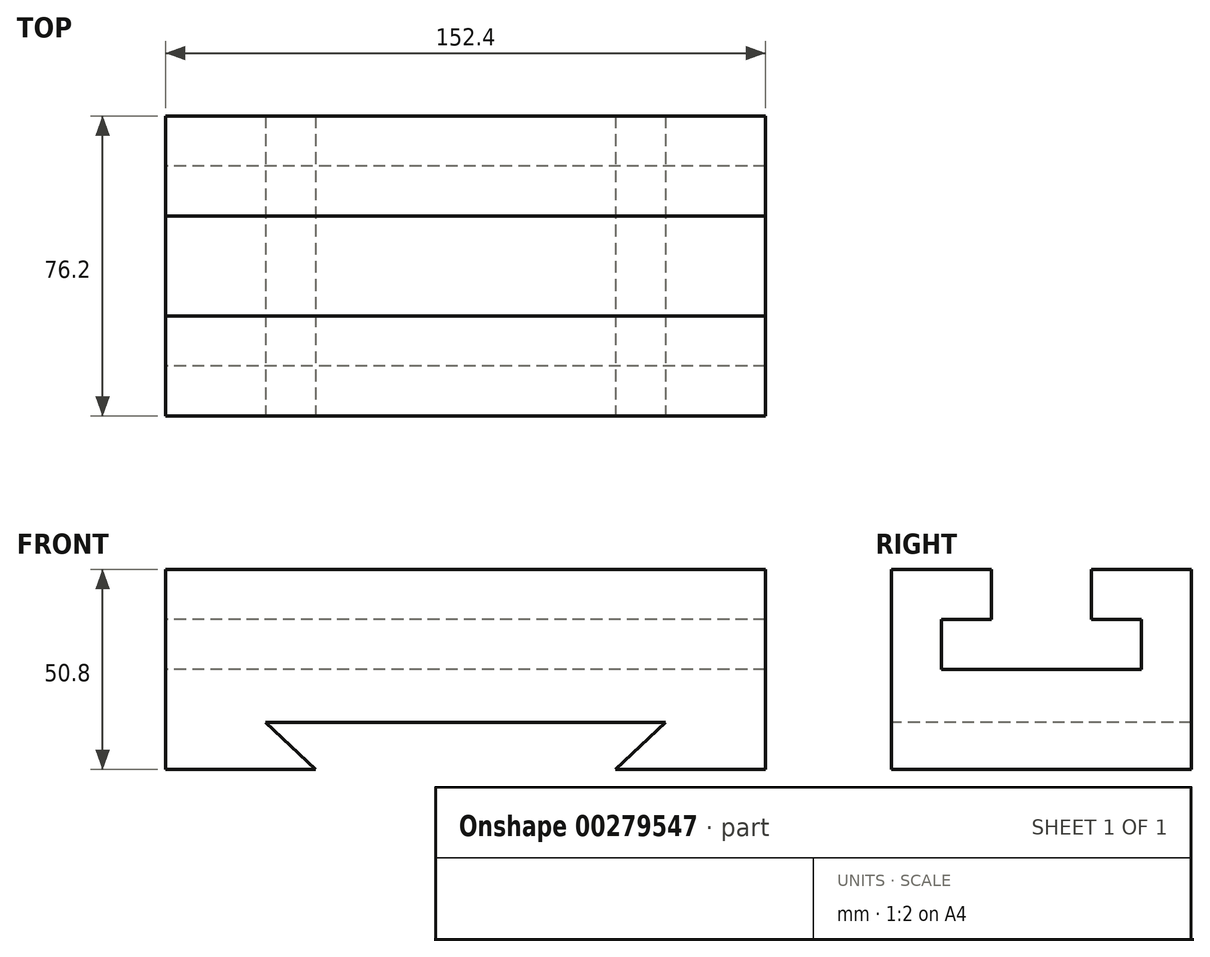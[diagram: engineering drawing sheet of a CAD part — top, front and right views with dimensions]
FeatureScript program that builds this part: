
annotation { "Feature Type Name" : "Feature", "Feature Type Description" : "" }
export const myFeature = defineFeature(function(context is Context, id is Id, definition is map)
    precondition{}
    {
        {
            var Q0;
            Q0=qCreatedBy(makeId("Right.planeOp"),FACE);
            var sketch = newSketch(context, id + "F0", { "sketchPlane" : qUnion([Q0])});
            skLineSegment(sketch, "E0.bottom", {"start": v(-38.1, 25.4) * mm, "end": v(-12.7, 25.4) * mm});
            skLineSegment(sketch, "E0.top", {"start": v(-38.1, -25.4) * mm, "end": v(38.1, -25.4) * mm});
            skLineSegment(sketch, "E0.left", {"start": v(-38.1, 25.4) * mm, "end": v(-38.1, -25.4) * mm});
            skLineSegment(sketch, "E0.right", {"start": v(38.1, 25.4) * mm, "end": v(38.1, -25.4) * mm});
            skPoint(sketch, "E0.middle", {"position": v(0, 0) * mm});
            skPoint(sketch, "E1", {"position": v(0, 25.4) * mm});
            skLineSegment(sketch, "E2", {"start": v(12.7, 25.4) * mm, "end": v(12.7, 12.7) * mm});
            skLineSegment(sketch, "E3", {"start": v(12.7, 12.7) * mm, "end": v(25.4, 12.7) * mm});
            skLineSegment(sketch, "E4", {"start": v(25.4, 12.7) * mm, "end": v(25.4, 0) * mm});
            skLineSegment(sketch, "E5", {"start": v(25.4, 0) * mm, "end": v(-25.4, 0) * mm});
            skLineSegment(sketch, "E6", {"start": v(-25.4, 0) * mm, "end": v(-25.4, 12.7) * mm});
            skLineSegment(sketch, "E7", {"start": v(-25.4, 12.7) * mm, "end": v(-12.7, 12.7) * mm});
            skLineSegment(sketch, "E8", {"start": v(-12.7, 12.7) * mm, "end": v(-12.7, 25.4) * mm});
            skLineSegment(sketch, "E9.trimOffspring", {"start": v(12.7, 25.4) * mm, "end": v(38.1, 25.4) * mm});
            skSolve(sketch);
        }
        {
            var Q0;
            Q0 = qSketchRegion(id + "F0", true);
            extrude(context, id + "F1", {"entities" : qUnion([Q0]), "depth" : 152.4 * mm});
        }
        {
            var Q0;
            Q0=qCreatedBy(makeId("Front.planeOp"),FACE);
            var sketch = newSketch(context, id + "F2", { "sketchPlane" : qUnion([Q0])});
            skPoint(sketch, "E10", {"position": v(76.2, -25.4) * mm});
            skLineSegment(sketch, "E11", {"start": v(38.1, -25.4) * mm, "end": v(114.3, -25.4) * mm});
            skLineSegment(sketch, "E12", {"start": v(93.65, -26.27) * mm, "end": v(93.65, -25.4) * mm});
            skLineSegment(sketch, "E13", {"start": v(38.1, -25.4) * mm, "end": v(25.4, -13.42) * mm});
            skLineSegment(sketch, "E14", {"start": v(25.4, -13.42) * mm, "end": v(127, -13.42) * mm});
            skLineSegment(sketch, "E15", {"start": v(127, -13.42) * mm, "end": v(114.3, -25.4) * mm});
            skPoint(sketch, "E16.orphan", {"position": v(93.65, -13.42) * mm});
            skSolve(sketch);
        }
        {
            var Q0;
            Q0 = qSketchRegion(id + "F2", true);
            extrude(context, id + "F3", {"entities" : qUnion([Q0]), "operationType" : NewBodyOperationType.REMOVE, "oppositeDirection" : true, "depth" : 76.2 * mm});
        }
        {
            var Q0;
            Q0=makeQuery(id+"F3.boolean.opBoolean","COPY",FACE,{"derivedFrom":makeQuery(id+"F3.opExtrude","CAP_FACE",FACE,{"disambiguationData":[OSD([sQuery(id+"F2.wireOp",EDGE,"E11"),sQuery(id+"F2.wireOp",EDGE,"E13"),sQuery(id+"F2.wireOp",EDGE,"E14"),sQuery(id+"F2.wireOp",EDGE,"E15")])],"isStart":true})});
            var sketch = newSketch(context, id + "F4", { "sketchPlane" : qUnion([Q0])});
            skPoint(sketch, "E17", {"position": v(-76.2, -25.4) * mm});
            skLineSegment(sketch, "E18", {"start": v(-38.1, -25.4) * mm, "end": v(-114.3, -25.4) * mm});
            skPoint(sketch, "E19", {"position": v(-76.2, -13.42) * mm});
            skPoint(sketch, "E20.orphan", {"position": v(-114.3, -13.42) * mm});
            skPoint(sketch, "E21.end.orphan", {"position": v(-38.1, -13.42) * mm});
            skLineSegment(sketch, "E22", {"start": v(-38.1, -25.4) * mm, "end": v(-25.4, -13.42) * mm});
            skLineSegment(sketch, "E23", {"start": v(-25.4, -13.42) * mm, "end": v(-127, -13.42) * mm});
            skLineSegment(sketch, "E24", {"start": v(-127, -13.42) * mm, "end": v(-114.3, -25.4) * mm});
            skSolve(sketch);
        }
        {
            var Q0;
            Q0 = qSketchRegion(id + "F4", true);
            extrude(context, id + "F5", {"entities" : qUnion([Q0]), "operationType" : NewBodyOperationType.REMOVE, "oppositeDirection" : true, "depth" : 76.2 * mm});
        }
    });
